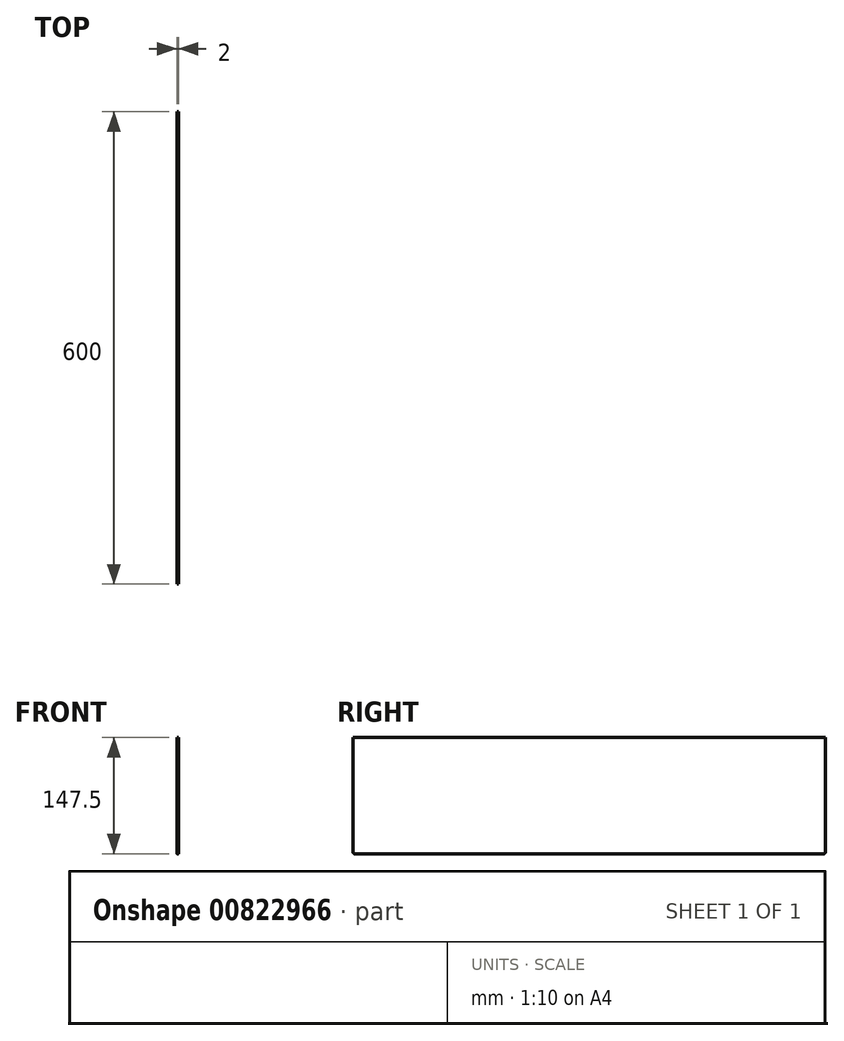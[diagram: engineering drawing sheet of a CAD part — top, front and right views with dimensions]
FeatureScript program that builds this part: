
annotation { "Feature Type Name" : "Feature", "Feature Type Description" : "" }
export const myFeature = defineFeature(function(context is Context, id is Id, definition is map)
    precondition{}
    {
        {
            var Q0;
            Q0=qCreatedBy(makeId("Right.planeOp"),FACE);
            var sketch = newSketch(context, id + "F0", { "sketchPlane" : qUnion([Q0])});
            skLineSegment(sketch, "E0.bottom", {"start": v(-300, -73.75) * mm, "end": v(300, -73.75) * mm});
            skLineSegment(sketch, "E0.top", {"start": v(-300, 73.75) * mm, "end": v(300, 73.75) * mm});
            skLineSegment(sketch, "E0.left", {"start": v(-300, -73.75) * mm, "end": v(-300, 73.75) * mm});
            skLineSegment(sketch, "E0.right", {"start": v(300, -73.75) * mm, "end": v(300, 73.75) * mm});
            skPoint(sketch, "E0.middle", {"position": v(0, 0) * mm});
            skSolve(sketch);
        }
        {
            var Q0;
            Q0=qSketchRegion(id+"F0",true);
            extrude(context, id + "F1", {"entities" : qUnion([Q0]), "depth" : 2 * mm, "offsetDistance" : 25 * mm});
        }
        {
            var Q0;
            Q0=makeQuery(id+"F1.opExtrude","SWEPT_EDGE",EDGE,{"disambiguationData":[OSD([sQuery(id+"F0.wireOp",EDGE,"E0.bottom"),sQuery(id+"F0.wireOp",EDGE,"E0.left")])]});
            var Q1;
            Q1=makeQuery(id+"F1.opExtrude","SWEPT_EDGE",EDGE,{"disambiguationData":[OSD([sQuery(id+"F0.wireOp",EDGE,"E0.bottom"),sQuery(id+"F0.wireOp",EDGE,"E0.right")])]});
            fillet(context, id + "F2", {"entities" : qUnion([Q0, Q1]), "radius" : 2 * mm, "tangentPropagation" : true, "allowEdgeOverflow" : false});
        }
    });
